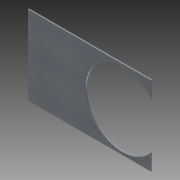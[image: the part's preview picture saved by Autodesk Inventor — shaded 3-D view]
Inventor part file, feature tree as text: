
AUTODESK INVENTOR PART (.ipt)
format: ipt  version: 2011 SP1 (Build 150282100, 282)  size: 86,528 bytes
history: native  units: in
note: dims shown in document units (in); Inventor stores cm internally (conversion verified against a paired STEP export)
features: extrude x1, hole x1, sketch x1
ambient origin geometry x8: Origin, YZ Plane, XZ Plane, XY Plane, X Axis, Y Axis, Z Axis, Center Point
bodies: Solid1 (feature_tree)
feature tree (3):
  extrude  "Extrusion1"  Depth=9.0in
  hole  "Hole1"  [1 undecoded]
  sketch  "Sketch1"  dims[d0=14.0in d1=9.0in d2=4.5in d3=6.0in d4=0.125in d5=0.0in d6=4.5in d7=3.25in d8=8.375in d9=0.75in d10=0.375in d11=0.25in d12=0.5635in d13=0.125in d14=0.8108in]
note: 1 required parameter value undecoded (feature->parameter linkage not recoverable at this tier; creation-order binding heuristic only, values carry confidence <= 0.55)
